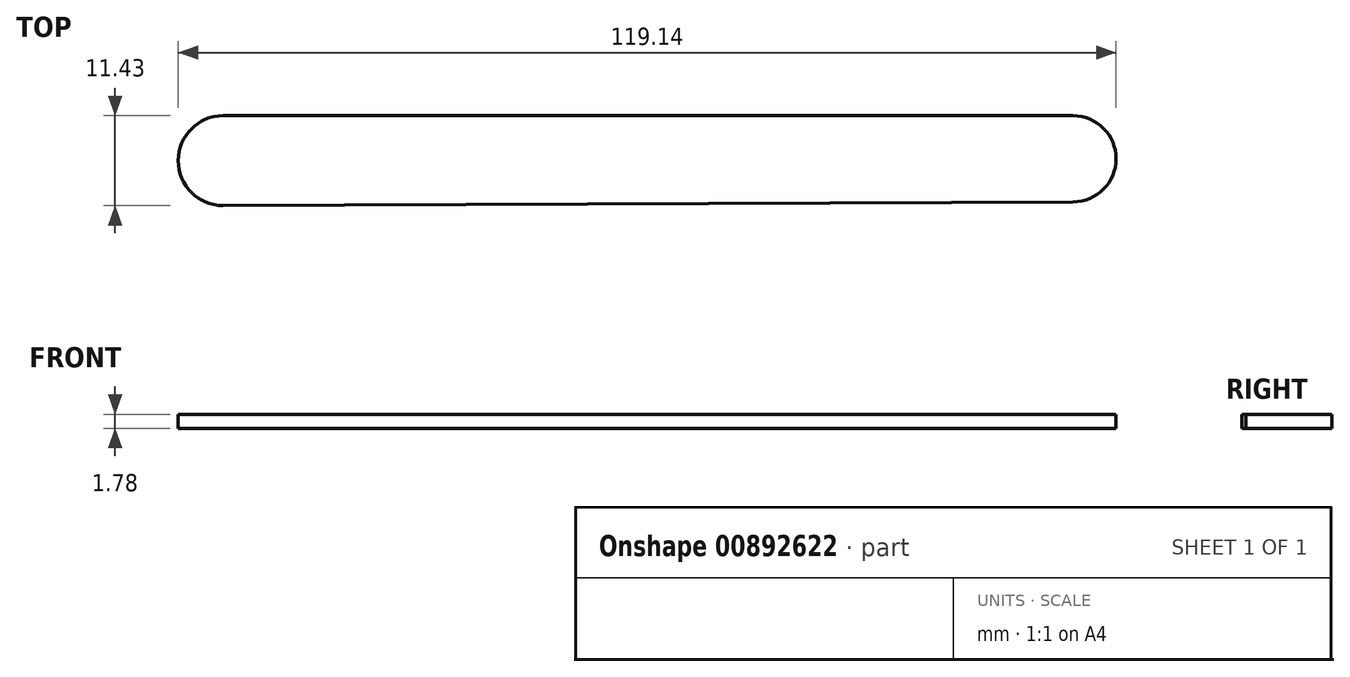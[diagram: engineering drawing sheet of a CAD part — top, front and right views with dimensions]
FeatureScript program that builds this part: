
annotation { "Feature Type Name" : "Feature", "Feature Type Description" : "" }
export const myFeature = defineFeature(function(context is Context, id is Id, definition is map)
    precondition{}
    {
        {
            var Q0;
            Q0=qCreatedBy(makeId("Top.planeOp"),FACE);
            var sketch = newSketch(context, id + "F0", { "sketchPlane" : qUnion([Q0])});
            skLineSegment(sketch, "E0", {"start": v(-52.04, 23.02) * mm, "end": v(55.9, 23.02) * mm});
            skLineSegment(sketch, "E1", {"start": v(55.9, 12.08) * mm, "end": v(-52.04, 11.59) * mm});
            skArc(sketch, "E2", {"start": v(-52.04, 23.02) * mm, "mid": v(-57.76, 17.3) * mm, "end": v(-52.04, 11.59) * mm});
            skArc(sketch, "E3", {"start": v(55.9, 23.02) * mm, "mid": v(61.38, 17.55) * mm, "end": v(55.9, 12.08) * mm});
            skSolve(sketch);
        }
        {
            var Q0;
            Q0=qSketchRegion(id+"F0",true);
            extrude(context, id + "F1", {"entities" : qUnion([Q0]), "depth" : 1.78 * mm, "offsetDistance" : 25.4 * mm});
        }
    });
